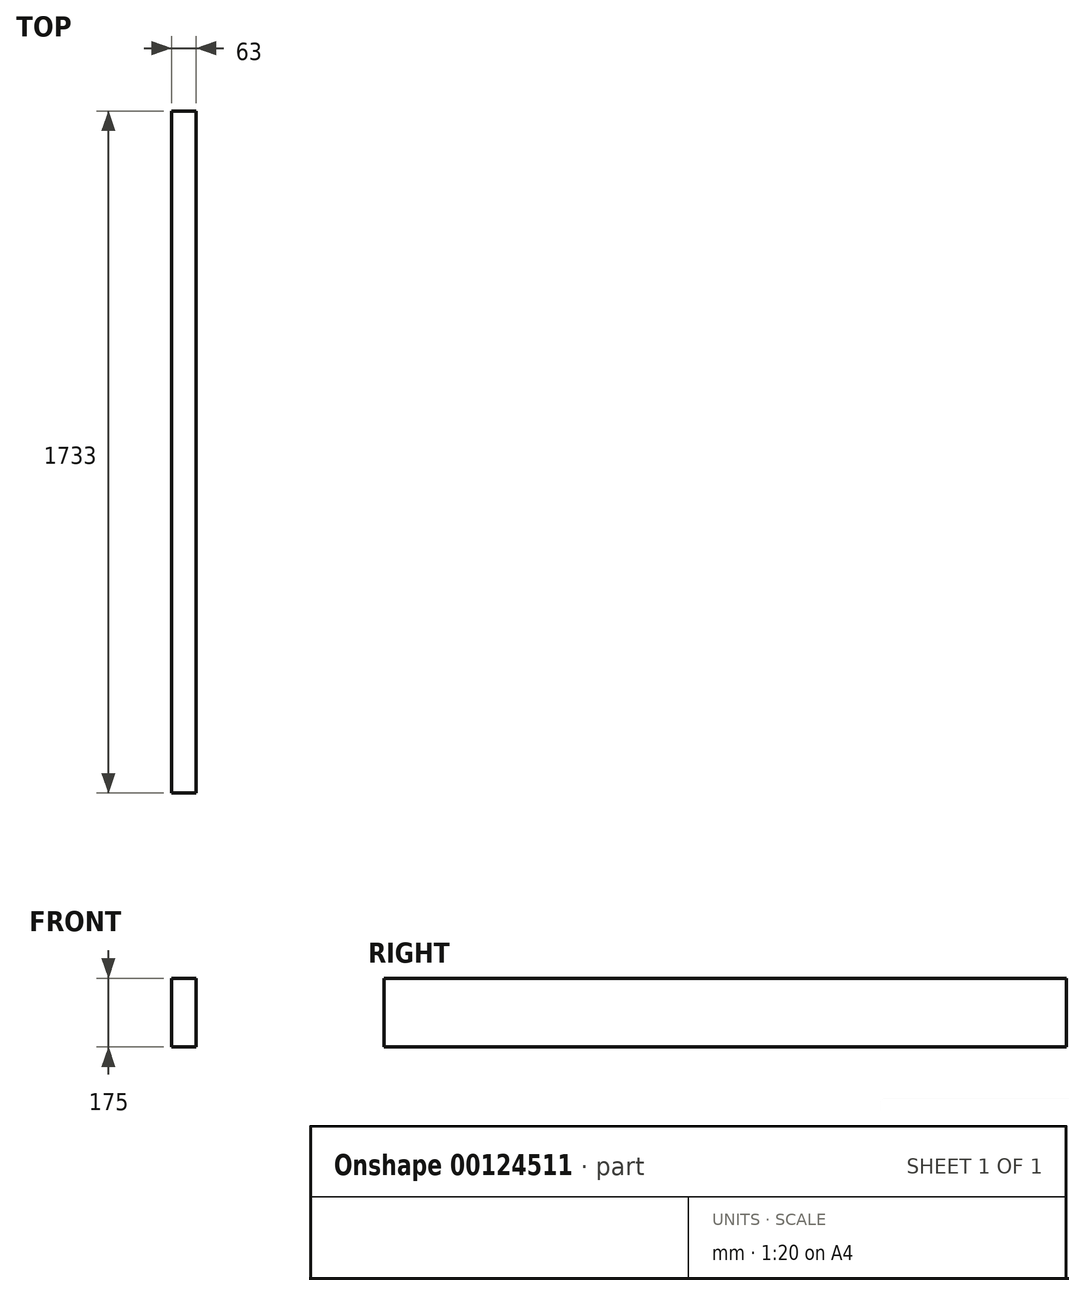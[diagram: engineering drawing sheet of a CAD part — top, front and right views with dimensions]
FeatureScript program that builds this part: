
annotation { "Feature Type Name" : "Feature", "Feature Type Description" : "" }
export const myFeature = defineFeature(function(context is Context, id is Id, definition is map)
    precondition{}
    {
        {
            var Q0;
            Q0=qCreatedBy(makeId("Front.planeOp"),FACE);
            var sketch = newSketch(context, id + "F0", { "sketchPlane" : qUnion([Q0])});
            skLineSegment(sketch, "E0.bottom", {"start": v(31.5, 87.5) * mm, "end": v(-31.5, 87.5) * mm});
            skLineSegment(sketch, "E0.top", {"start": v(31.5, -87.5) * mm, "end": v(-31.5, -87.5) * mm});
            skLineSegment(sketch, "E0.left", {"start": v(31.5, 87.5) * mm, "end": v(31.5, -87.5) * mm});
            skLineSegment(sketch, "E0.right", {"start": v(-31.5, 87.5) * mm, "end": v(-31.5, -87.5) * mm});
            skPoint(sketch, "E0.middle", {"position": v(0, 0) * mm});
            skSolve(sketch);
        }
        {
            var Q0;
            Q0 = qSketchRegion(id + "F0", true);
            extrude(context, id + "F1", {"entities" : qUnion([Q0]), "endBound" : BoundingType.SYMMETRIC, "depth" : (1450 + 323 - 40) * mm});
        }
    });
